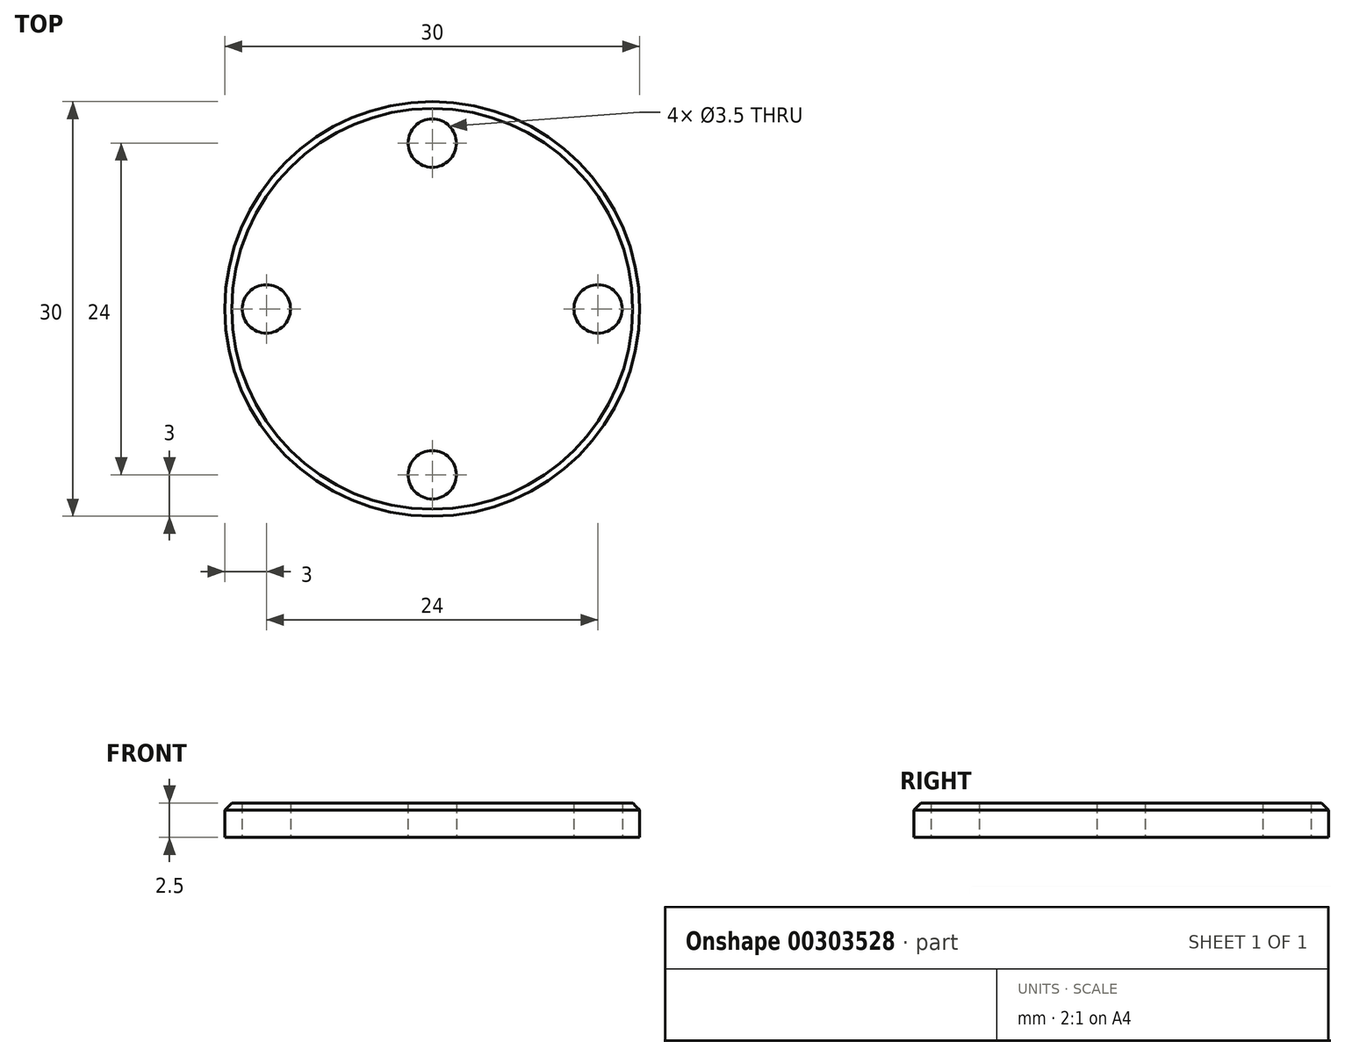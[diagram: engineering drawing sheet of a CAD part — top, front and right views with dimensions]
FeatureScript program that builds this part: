
annotation { "Feature Type Name" : "Feature", "Feature Type Description" : "" }
export const myFeature = defineFeature(function(context is Context, id is Id, definition is map)
    precondition{}
    {
        {
            var Q0;
            Q0=qCreatedBy(makeId("Top.planeOp"),FACE);
            var sketch = newSketch(context, id + "F0", { "sketchPlane" : qUnion([Q0])});
            skCircle(sketch, "E0", {"center": v(0, 0) * mm, "radius": 15 * mm});
            skCircle(sketch, "E1", {"center": v(0, 0) * mm, "radius": 6.5 * mm});
            skCircle(sketch, "E2", {"center": v(0, 0) * mm, "radius": 12 * mm, "construction": true});
            skCircle(sketch, "E3", {"center": v(0, 12) * mm, "radius": 1.75 * mm});
            skCircle(sketch, "E4.1.0", {"center": v(-12, 0) * mm, "radius": 1.75 * mm});
            skCircle(sketch, "E4.2.0", {"center": v(0, -12) * mm, "radius": 1.75 * mm});
            skCircle(sketch, "E4.3.0", {"center": v(12, 0) * mm, "radius": 1.75 * mm});
            skSolve(sketch);
        }
        {
            var Q0;
            Q0=makeQuery(id+"F0.imprint","IMPRINT",FACE,{"disambiguationData":[TD([[makeQuery(id+"F0.imprint","IMPRINT",EDGE,{"derivedFrom":sQuery(id+"F0.wireOp",EDGE,"E0")}),1.0]])]});
            var Q1;
            Q1=makeQuery(id+"F0.imprint","IMPRINT",FACE,{"disambiguationData":[TD([[makeQuery(id+"F0.imprint","IMPRINT",EDGE,{"derivedFrom":sQuery(id+"F0.wireOp",EDGE,"E1")}),1.0]])]});
            extrude(context, id + "F1", {"entities" : qUnion([Q0, Q1]), "depth" : 2.5 * mm});
        }
        {
            var Q0;
            Q0=makeQuery(id+"F1.opExtrude","CAP_EDGE",EDGE,{"disambiguationData":[OSD([sQuery(id+"F0.wireOp",EDGE,"E0")])],"isStart":false});
            chamfer(context, id + "F2", {"entities" : qUnion([Q0]), "width" : 0.5 * mm, "tangentPropagation" : true});
        }
    });
